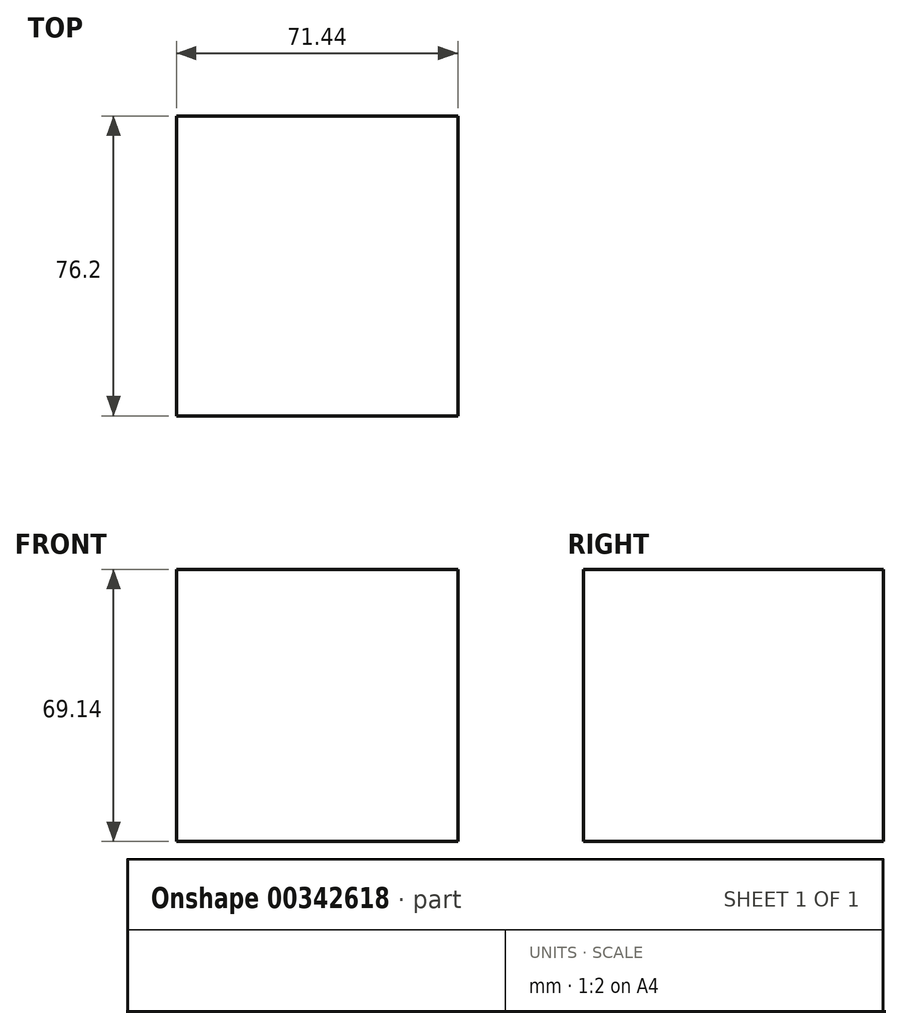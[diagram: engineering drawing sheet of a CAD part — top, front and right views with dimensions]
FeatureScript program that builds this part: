
annotation { "Feature Type Name" : "Feature", "Feature Type Description" : "" }
export const myFeature = defineFeature(function(context is Context, id is Id, definition is map)
    precondition{}
    {
        {
            var Q0;
            Q0=qCreatedBy(makeId("Front.planeOp"),FACE);
            var sketch = newSketch(context, id + "F0", { "sketchPlane" : qUnion([Q0])});
            skLineSegment(sketch, "E0.bottom", {"start": v(23.02, 21.87) * mm, "end": v(-23.02, 21.87) * mm});
            skLineSegment(sketch, "E0.top", {"start": v(23.02, -21.87) * mm, "end": v(-23.02, -21.87) * mm});
            skLineSegment(sketch, "E0.left", {"start": v(23.02, 21.87) * mm, "end": v(23.02, -21.87) * mm});
            skLineSegment(sketch, "E0.right", {"start": v(-23.02, 21.87) * mm, "end": v(-23.02, -21.87) * mm});
            skPoint(sketch, "E0.middle", {"position": v(0, 0) * mm});
            skSolve(sketch);
        }
        {
            var Q0;
            Q0 = qSketchRegion(id + "F0", true);
            extrude(context, id + "F1", {"entities" : qUnion([Q0]), "depth" : 50.8 * mm});
        }
        {
            var Q0;
            Q0=makeQuery(id+"F1.opExtrude","CAP_FACE",FACE,{"disambiguationData":[OSD([sQuery(id+"F0.wireOp",EDGE,"E0.bottom"),sQuery(id+"F0.wireOp",EDGE,"E0.top"),sQuery(id+"F0.wireOp",EDGE,"E0.left"),sQuery(id+"F0.wireOp",EDGE,"E0.right")])],"isStart":false});
            extrude(context, id + "F2", {"entities" : qUnion([Q0]), "operationType" : NewBodyOperationType.ADD, "depth" : 25.4 * mm});
        }
        {
            var Q0;
            {var subQ0=sQuery(id+"F0.wireOp",EDGE,"E0.top");Q0=makeQuery(id+"F2.boolean.opBoolean","MERGE",FACE,{"derivedFrom":[makeQuery(id+"F1.opExtrude","SWEPT_FACE",FACE,{"disambiguationData":[OSD([subQ0])]}),makeQuery(id+"F2.opExtrude","SWEPT_FACE",FACE,{"disambiguationData":[OSD([subQ0])]})]});}
            extrude(context, id + "F3", {"entities" : qUnion([Q0]), "operationType" : NewBodyOperationType.ADD, "depth" : 25.4 * mm});
        }
        {
            var Q0;
            {var subQ0=sQuery(id+"F0.wireOp",EDGE,"E0.right");Q0=makeQuery(id+"F3.boolean.opBoolean","MERGE",FACE,{"derivedFrom":[makeQuery(id+"F2.boolean.opBoolean","MERGE",FACE,{"derivedFrom":[makeQuery(id+"F1.opExtrude","SWEPT_FACE",FACE,{"disambiguationData":[OSD([subQ0])]}),makeQuery(id+"F2.opExtrude","SWEPT_FACE",FACE,{"disambiguationData":[OSD([subQ0])]})]}),makeQuery(id+"F3.opExtrude","SWEPT_FACE",FACE,{"disambiguationData":[OSD([sQuery(id+"F0.wireOp",EDGE,"E0.top"),subQ0])]})]});}
            extrude(context, id + "F4", {"entities" : qUnion([Q0]), "operationType" : NewBodyOperationType.ADD, "depth" : 25.4 * mm});
        }
    });
